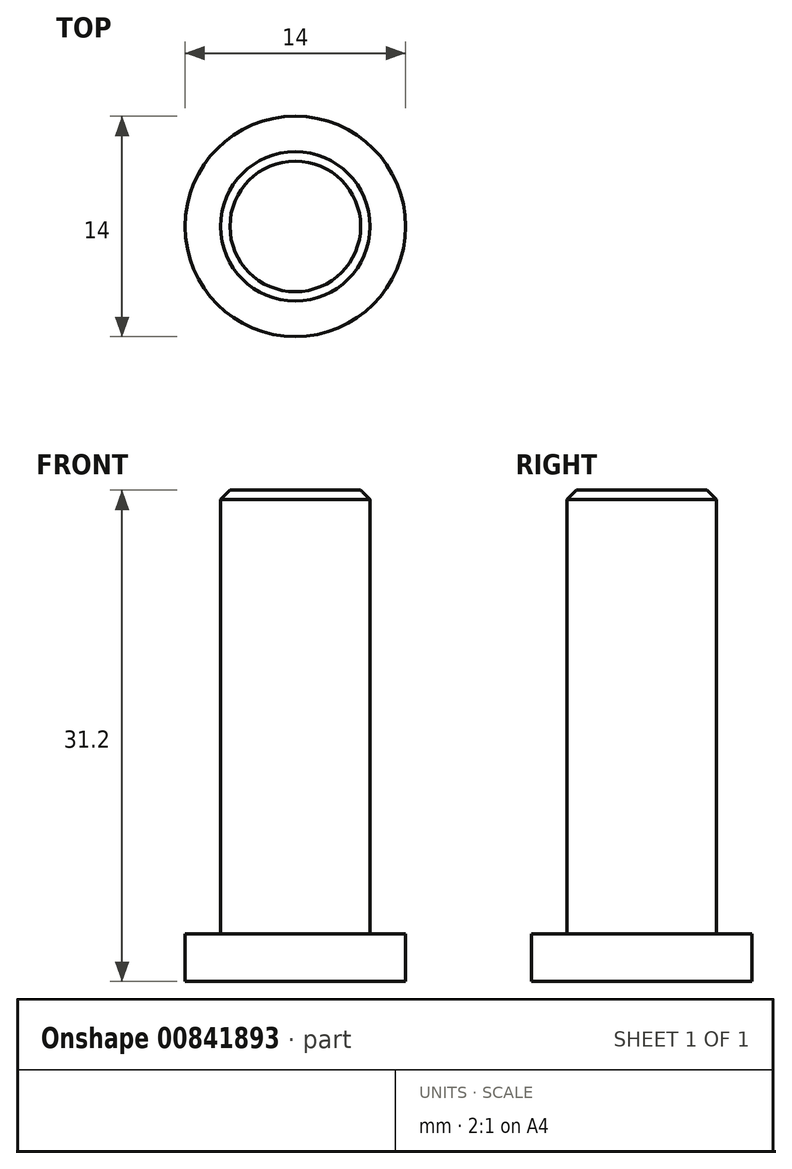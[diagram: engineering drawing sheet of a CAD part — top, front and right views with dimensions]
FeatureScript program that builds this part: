
annotation { "Feature Type Name" : "Feature", "Feature Type Description" : "" }
export const myFeature = defineFeature(function(context is Context, id is Id, definition is map)
    precondition{}
    {
        {
            var Q0;
            Q0=qCreatedBy(makeId("Top.planeOp"),FACE);
            var sketch = newSketch(context, id + "F0", { "sketchPlane" : qUnion([Q0])});
            skCircle(sketch, "E0", {"center": v(0, 0) * mm, "radius": 4.75 * mm});
            skCircle(sketch, "E1", {"center": v(0, 0) * mm, "radius": 7 * mm});
            skSolve(sketch);
        }
        {
            var Q0;
            Q0=makeQuery(id+"F0.imprint","IMPRINT",FACE,{"disambiguationData":[TD([[makeQuery(id+"F0.imprint","IMPRINT",EDGE,{"derivedFrom":sQuery(id+"F0.wireOp",EDGE,"E0")}),1.0]])]});
            extrude(context, id + "F1", {"entities" : qUnion([Q0]), "depth" : 31.2 * mm, "offsetDistance" : 25 * mm});
        }
        {
            var Q0;
            Q0=makeQuery(id+"F0.imprint","IMPRINT",FACE,{"disambiguationData":[TD([[makeQuery(id+"F0.imprint","IMPRINT",EDGE,{"derivedFrom":sQuery(id+"F0.wireOp",EDGE,"E0")}),-1.0]])]});
            extrude(context, id + "F2", {"entities" : qUnion([Q0]), "operationType" : NewBodyOperationType.ADD, "depth" : 3 * mm, "offsetDistance" : 25 * mm});
        }
        {
            var Q0;
            Q0=makeQuery(id+"F1.opExtrude","CAP_EDGE",EDGE,{"disambiguationData":[OSD([sQuery(id+"F0.wireOp",EDGE,"E0")])],"isStart":false});
            chamfer(context, id + "F3", {"entities" : qUnion([Q0]), "width" : 0.6 * mm, "tangentPropagation" : true});
        }
    });
